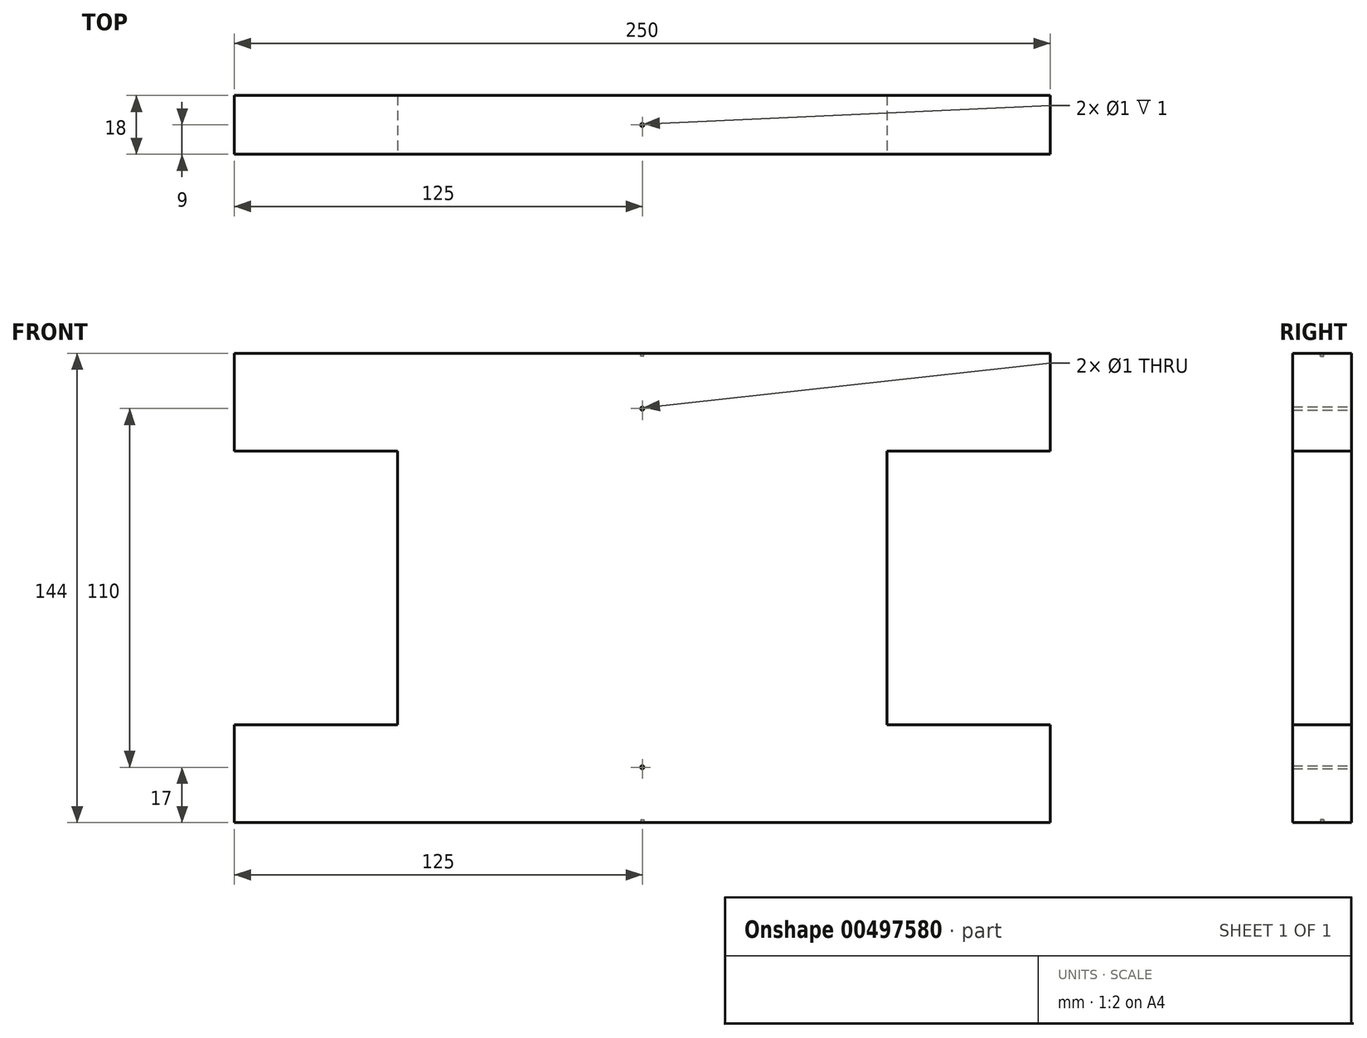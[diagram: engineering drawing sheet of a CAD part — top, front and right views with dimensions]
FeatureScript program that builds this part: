
annotation { "Feature Type Name" : "Feature", "Feature Type Description" : "" }
export const myFeature = defineFeature(function(context is Context, id is Id, definition is map)
    precondition{}
    {
        {
            var Q0;
            Q0=qCreatedBy(makeId("Front.planeOp"),FACE);
            var sketch = newSketch(context, id + "F0", { "sketchPlane" : qUnion([Q0])});
            skLineSegment(sketch, "E0.bottom", {"start": v(0, 0) * mm, "end": v(150, 0) * mm});
            skLineSegment(sketch, "E0.top", {"start": v(0, 144) * mm, "end": v(150, 144) * mm});
            skLineSegment(sketch, "E0.left", {"start": v(0, 0) * mm, "end": v(0, 144) * mm});
            skLineSegment(sketch, "E0.right", {"start": v(150, 0) * mm, "end": v(150, 144) * mm});
            skPoint(sketch, "E1.centerSnap0", {"position": v(75, 144) * mm});
            skLineSegment(sketch, "E2", {"start": v(0, 72) * mm, "end": v(150, 72) * mm, "construction": true});
            skCircle(sketch, "E3", {"center": v(75, 17) * mm, "radius": 0.5 * mm});
            skPoint(sketch, "E3.centerSnap0", {"position": v(75, 72) * mm});
            skCircle(sketch, "E4.MirrorC", {"center": v(75, 127) * mm, "radius": 0.5 * mm});
            skSolve(sketch);
        }
        {
            var Q0;
            Q0=qSketchRegion(id+"F0",true);
            extrude(context, id + "F1", {"entities" : qUnion([Q0]), "depth" : 18 * mm, "offsetDistance" : 25.4 * mm});
        }
        {
            var Q0;
            Q0=makeQuery(id+"F1.opExtrude","SWEPT_FACE",FACE,{"disambiguationData":[OSD([sQuery(id+"F0.wireOp",EDGE,"E0.bottom")])]});
            var sketch = newSketch(context, id + "F2", { "sketchPlane" : qUnion([Q0])});
            skCircle(sketch, "E5", {"center": v(75, 9) * mm, "radius": 0.5 * mm});
            skPoint(sketch, "E5.centerSnap0", {"position": v(75, 0) * mm});
            skPoint(sketch, "E5.centerSnap1", {"position": v(0, 9) * mm});
            skSolve(sketch);
        }
        {
            var Q0;
            Q0=qSketchRegion(id+"F2",true);
            extrude(context, id + "F3", {"entities" : qUnion([Q0]), "operationType" : NewBodyOperationType.REMOVE, "oppositeDirection" : true, "depth" : 1 * mm, "offsetDistance" : 25.4 * mm});
        }
        {
            var Q0;
            Q0=makeQuery(id+"F1.opExtrude","SWEPT_FACE",FACE,{"disambiguationData":[OSD([sQuery(id+"F0.wireOp",EDGE,"E0.top")])]});
            var sketch = newSketch(context, id + "F4", { "sketchPlane" : qUnion([Q0])});
            skCircle(sketch, "E6", {"center": v(75, -9) * mm, "radius": 0.5 * mm});
            skPoint(sketch, "E6.centerSnap0", {"position": v(75, -18) * mm});
            skPoint(sketch, "E6.centerSnap1", {"position": v(0, -9) * mm});
            skSolve(sketch);
        }
        {
            var Q0;
            Q0=qSketchRegion(id+"F4",true);
            extrude(context, id + "F5", {"entities" : qUnion([Q0]), "operationType" : NewBodyOperationType.REMOVE, "oppositeDirection" : true, "depth" : 1 * mm, "offsetDistance" : 25.4 * mm});
        }
        {
            var Q0;
            Q0=makeQuery(id+"F1.opExtrude","SWEPT_FACE",FACE,{"disambiguationData":[OSD([sQuery(id+"F0.wireOp",EDGE,"E0.left")])]});
            var sketch = newSketch(context, id + "F6", { "sketchPlane" : qUnion([Q0])});
            skLineSegment(sketch, "E7.bottom", {"start": v(0, 144) * mm, "end": v(18, 144) * mm});
            skLineSegment(sketch, "E7.top", {"start": v(0, 114) * mm, "end": v(18, 114) * mm});
            skLineSegment(sketch, "E7.left", {"start": v(0, 144) * mm, "end": v(0, 114) * mm});
            skLineSegment(sketch, "E7.right", {"start": v(18, 144) * mm, "end": v(18, 114) * mm});
            skLineSegment(sketch, "E8", {"start": v(0, 72) * mm, "end": v(18, 72) * mm, "construction": true});
            skLineSegment(sketch, "E9.MirrorCS", {"start": v(0, 0) * mm, "end": v(18, 0) * mm});
            skLineSegment(sketch, "E10.MirrorCS", {"start": v(0, 30) * mm, "end": v(18, 30) * mm});
            skLineSegment(sketch, "E11.MirrorCS", {"start": v(0, 0) * mm, "end": v(0, 30) * mm});
            skLineSegment(sketch, "E12.MirrorCS", {"start": v(18, 0) * mm, "end": v(18, 30) * mm});
            skSolve(sketch);
        }
        {
            var Q0;
            Q0=qSketchRegion(id+"F6",true);
            extrude(context, id + "F7", {"entities" : qUnion([Q0]), "operationType" : NewBodyOperationType.ADD, "depth" : 50 * mm, "offsetDistance" : 25.4 * mm});
        }
        {
            var Q0;
            Q0=makeQuery(id+"F1.opExtrude","SWEPT_FACE",FACE,{"disambiguationData":[OSD([sQuery(id+"F0.wireOp",EDGE,"E0.right")])]});
            var sketch = newSketch(context, id + "F8", { "sketchPlane" : qUnion([Q0])});
            skLineSegment(sketch, "E13.bottom", {"start": v(0, 0) * mm, "end": v(-18, 0) * mm});
            skLineSegment(sketch, "E13.top", {"start": v(0, 30) * mm, "end": v(-18, 30) * mm});
            skLineSegment(sketch, "E13.left", {"start": v(0, 0) * mm, "end": v(0, 30) * mm});
            skLineSegment(sketch, "E13.right", {"start": v(-18, 0) * mm, "end": v(-18, 30) * mm});
            skLineSegment(sketch, "E14", {"start": v(0, 72) * mm, "end": v(-18, 72) * mm, "construction": true});
            skLineSegment(sketch, "E15.MirrorCS", {"start": v(0, 144) * mm, "end": v(-18, 144) * mm});
            skLineSegment(sketch, "E16.MirrorCS", {"start": v(0, 114) * mm, "end": v(-18, 114) * mm});
            skLineSegment(sketch, "E17.MirrorCS", {"start": v(0, 144) * mm, "end": v(0, 114) * mm});
            skLineSegment(sketch, "E18.MirrorCS", {"start": v(-18, 144) * mm, "end": v(-18, 114) * mm});
            skSolve(sketch);
        }
        {
            var Q0;
            Q0=qSketchRegion(id+"F8",true);
            extrude(context, id + "F9", {"entities" : qUnion([Q0]), "operationType" : NewBodyOperationType.ADD, "depth" : 50 * mm, "offsetDistance" : 25.4 * mm});
        }
    });
